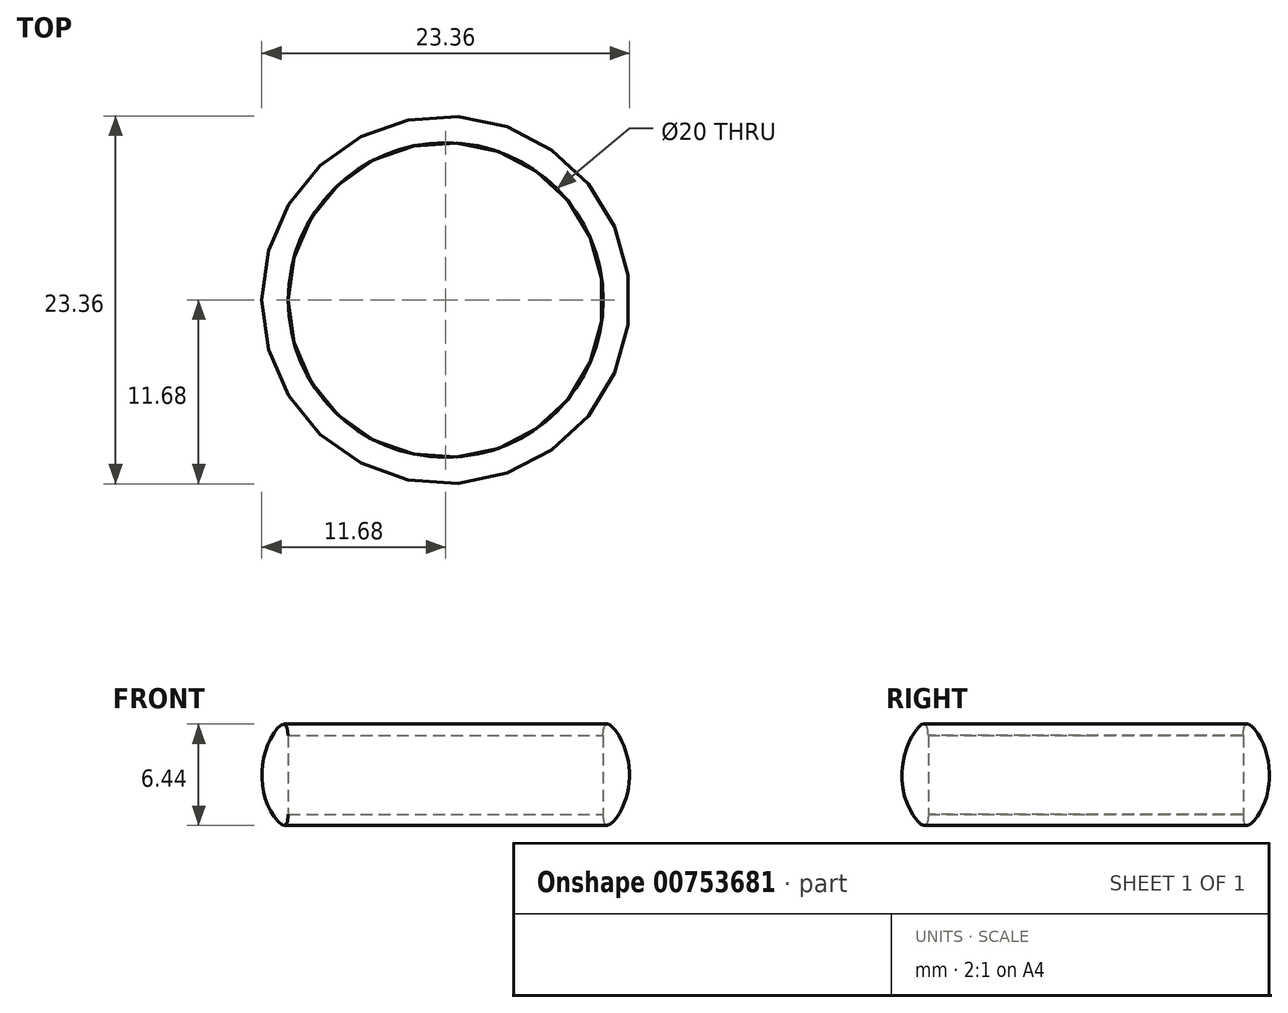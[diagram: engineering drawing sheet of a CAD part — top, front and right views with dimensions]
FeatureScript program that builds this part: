
annotation { "Feature Type Name" : "Feature", "Feature Type Description" : "" }
export const myFeature = defineFeature(function(context is Context, id is Id, definition is map)
    precondition{}
    {
        {
            var Q0;
            Q0=qCreatedBy(makeId("Front.planeOp"),FACE);
            var sketch = newSketch(context, id + "F0", { "sketchPlane" : qUnion([Q0])});
            skLineSegment(sketch, "E0", {"start": v(10, 0) * mm, "end": v(10, -5) * mm});
            skLineSegment(sketch, "E1", {"start": v(0, 0) * mm, "end": v(0, 18.5) * mm});
            skFitSpline(sketch, "E2", {"points": [v(10, 0) * mm, v(11, 0) * mm, v(11, -5) * mm, v(10, -5) * mm], "startDerivative": vector(0.37, 15.73) * mm, "endDerivative": vector(0.26, 15.3) * mm});
            skSolve(sketch);
        }
        {
            var Q0;
            Q0=qSketchRegion(id+"F0",true);
            var Q1;
            Q1=sQuery(id+"F0.wireOp",EDGE,"E1");
            revolve(context, id + "F1", {"surfaceOperationType" : NewSurfaceOperationType.NEW, "entities" : qUnion([Q0]), "axis" : qUnion([Q1]), "revolveType" : RevolveType.FULL});
        }
    });
